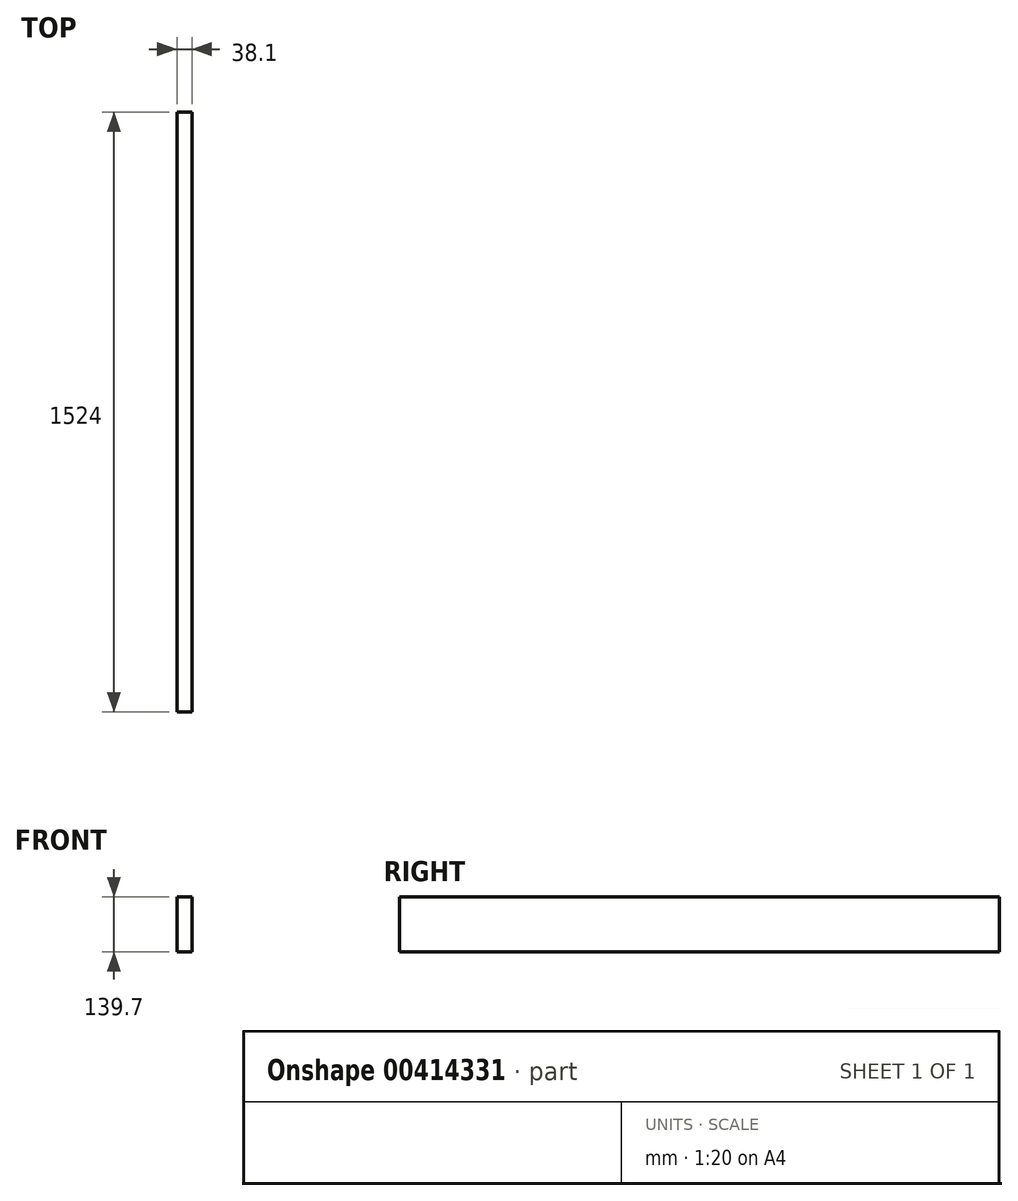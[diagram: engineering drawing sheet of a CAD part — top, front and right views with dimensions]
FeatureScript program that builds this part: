
annotation { "Feature Type Name" : "Feature", "Feature Type Description" : "" }
export const myFeature = defineFeature(function(context is Context, id is Id, definition is map)
    precondition{}
    {
        {
            var Q0;
            Q0=qCreatedBy(makeId("Top.planeOp"),FACE);
            var sketch = newSketch(context, id + "F0", { "sketchPlane" : qUnion([Q0])});
            skLineSegment(sketch, "E0.bottom", {"start": v(19.05, 762) * mm, "end": v(-19.05, 762) * mm});
            skLineSegment(sketch, "E0.top", {"start": v(19.05, -762) * mm, "end": v(-19.05, -762) * mm});
            skLineSegment(sketch, "E0.left", {"start": v(19.05, 762) * mm, "end": v(19.05, -762) * mm});
            skLineSegment(sketch, "E0.right", {"start": v(-19.05, 762) * mm, "end": v(-19.05, -762) * mm});
            skPoint(sketch, "E0.middle", {"position": v(0, 0) * mm});
            skSolve(sketch);
        }
        {
            var Q0;
            Q0 = qSketchRegion(id + "F0", true);
            extrude(context, id + "F1", {"entities" : qUnion([Q0]), "depth" : 139.7 * mm});
        }
    });
